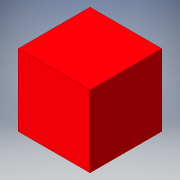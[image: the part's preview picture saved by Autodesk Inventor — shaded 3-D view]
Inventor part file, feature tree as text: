
AUTODESK INVENTOR PART (.ipt)
format: ipt  version: 2016 (Build 200138000, 138)  size: 96,256 bytes
history: native  units: in
note: dims shown in document units (in); Inventor stores cm internally (conversion verified against a paired STEP export)
features: extrude x1, sketch x1
ambient origin geometry x8: Origin, YZ Plane, XZ Plane, XY Plane, X Axis, Y Axis, Z Axis, Center Point
bodies: Solid1 (feature_tree)
feature tree (2):
  extrude  "Extrusion1"  Depth=1.0in
  sketch  "Sketch1"  dims[d0=1.0in d1=1.0in d2=1.0in d3=0.0in]
